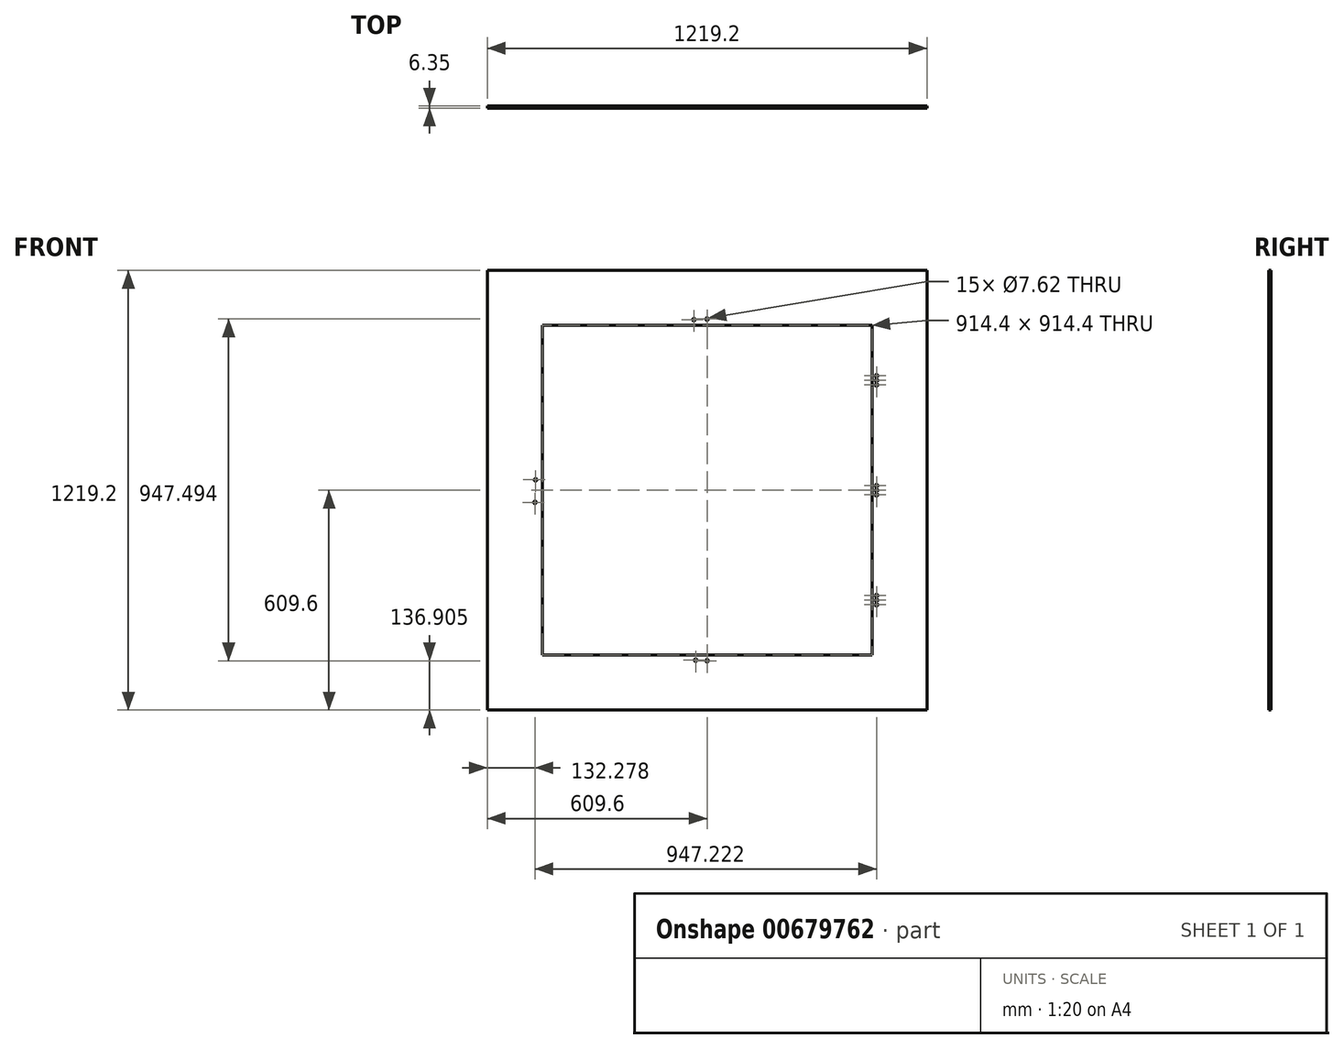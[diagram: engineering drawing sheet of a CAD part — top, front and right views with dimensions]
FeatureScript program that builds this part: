
annotation { "Feature Type Name" : "Feature", "Feature Type Description" : "" }
export const myFeature = defineFeature(function(context is Context, id is Id, definition is map)
    precondition{}
    {
        {
            var Q0;
            Q0=qCreatedBy(makeId("Front.planeOp"),FACE);
            var sketch = newSketch(context, id + "F0", { "sketchPlane" : qUnion([Q0])});
            skLineSegment(sketch, "E0.bottom", {"start": v(609.6, -609.6) * mm, "end": v(-609.6, -609.6) * mm});
            skLineSegment(sketch, "E0.top", {"start": v(609.6, 609.6) * mm, "end": v(-609.6, 609.6) * mm});
            skLineSegment(sketch, "E0.left", {"start": v(609.6, -609.6) * mm, "end": v(609.6, 609.6) * mm});
            skLineSegment(sketch, "E0.right", {"start": v(-609.6, -609.6) * mm, "end": v(-609.6, 609.6) * mm});
            skPoint(sketch, "E0.middle", {"position": v(0, 0) * mm});
            skLineSegment(sketch, "E1.bottom", {"start": v(457.2, -457.2) * mm, "end": v(-457.2, -457.2) * mm});
            skLineSegment(sketch, "E1.top", {"start": v(457.2, 457.2) * mm, "end": v(-457.2, 457.2) * mm});
            skLineSegment(sketch, "E1.left", {"start": v(457.2, -457.2) * mm, "end": v(457.2, 457.2) * mm});
            skLineSegment(sketch, "E1.right", {"start": v(-457.2, -457.2) * mm, "end": v(-457.2, 457.2) * mm});
            skLineSegment(sketch, "E2", {"start": v(469.9, 639.15) * mm, "end": v(469.9, -669.22) * mm});
            skLineSegment(sketch, "E3", {"start": v(300.82, 304.8) * mm, "end": v(457.2, 304.8) * mm});
            skLineSegment(sketch, "E4", {"start": v(303.39, 0) * mm, "end": v(457.2, 0) * mm});
            skLineSegment(sketch, "E5", {"start": v(313.4, -304.8) * mm, "end": v(457.2, -304.8) * mm});
            skPoint(sketch, "E6", {"position": v(469.9, 304.8) * mm});
            skPoint(sketch, "E7", {"position": v(469.9, 317.5) * mm});
            skPoint(sketch, "E8", {"position": v(469.9, 292.1) * mm});
            skPoint(sketch, "E9", {"position": v(469.9, 0) * mm});
            skPoint(sketch, "E10", {"position": v(469.9, 12.7) * mm});
            skPoint(sketch, "E11", {"position": v(469.9, -12.7) * mm});
            skPoint(sketch, "E12", {"position": v(469.9, -292.1) * mm});
            skPoint(sketch, "E13", {"position": v(469.9, -304.8) * mm});
            skPoint(sketch, "E14", {"position": v(469.9, -317.5) * mm});
            skLineSegment(sketch, "E15.trimOffspring", {"start": v(609.6, 304.8) * mm, "end": v(695.75, 304.8) * mm});
            skLineSegment(sketch, "E16.trimOffspring", {"start": v(609.6, 0) * mm, "end": v(667.54, 0) * mm});
            skLineSegment(sketch, "E17.trimOffspring", {"start": v(609.6, -304.8) * mm, "end": v(688.77, -304.8) * mm});
            skPoint(sketch, "E18", {"position": v(0, 474.8) * mm});
            skPoint(sketch, "E19", {"position": v(0, -472.7) * mm});
            skPoint(sketch, "E19.positionSnap0", {"position": v(0, -457.2) * mm});
            skPoint(sketch, "E20", {"position": v(-31.73, -471.09) * mm});
            skPoint(sketch, "E21", {"position": v(-477.32, -33.53) * mm});
            skPoint(sketch, "E22", {"position": v(-475.71, 29.2) * mm});
            skPoint(sketch, "E23", {"position": v(-36.55, 473.2) * mm});
            skSolve(sketch);
        }
        {
            var Q0;
            Q0 = qSketchRegion(id + "F0", true);
            extrude(context, id + "F1", {"entities" : qUnion([Q0]), "depth" : 6.35 * mm, "offsetDistance" : 30.48 * mm});
        }
        {
            var Q0;
            Q0=sQuery(id+"F0.wireOp",VERTEX,"E7");
            var Q1;
            Q1=sQuery(id+"F0.wireOp",VERTEX,"E6");
            var Q2;
            Q2=sQuery(id+"F0.wireOp",VERTEX,"E8");
            var Q3;
            Q3=sQuery(id+"F0.wireOp",VERTEX,"E10");
            var Q4;
            Q4=sQuery(id+"F0.wireOp",VERTEX,"E11");
            var Q5;
            Q5=sQuery(id+"F0.wireOp",VERTEX,"E9");
            var Q6;
            Q6=sQuery(id+"F0.wireOp",VERTEX,"E12");
            var Q7;
            Q7=sQuery(id+"F0.wireOp",VERTEX,"E13");
            var Q8;
            Q8=sQuery(id+"F0.wireOp",VERTEX,"E14");
            var Q9;
            Q9=sQuery(id+"F0.wireOp",VERTEX,"E18");
            var Q10;
            Q10=sQuery(id+"F0.wireOp",VERTEX,"E23");
            var Q11;
            Q11=sQuery(id+"F0.wireOp",VERTEX,"E22");
            var Q12;
            Q12=sQuery(id+"F0.wireOp",VERTEX,"E21");
            var Q13;
            Q13=sQuery(id+"F0.wireOp",VERTEX,"E20");
            var Q14;
            Q14=sQuery(id+"F0.wireOp",VERTEX,"E19");
            var Q15;
            Q15=makeQuery(id+"F1.opExtrude","SWEPT_BODY",BODY,{"disambiguationData":[OSD([sQuery(id+"F0.wireOp",EDGE,"E0.bottom"),sQuery(id+"F0.wireOp",EDGE,"E0.top"),sQuery(id+"F0.wireOp",EDGE,"E0.left"),sQuery(id+"F0.wireOp",EDGE,"E0.right"),sQuery(id+"F0.wireOp",EDGE,"E1.bottom"),sQuery(id+"F0.wireOp",EDGE,"E1.top"),sQuery(id+"F0.wireOp",EDGE,"E1.left"),sQuery(id+"F0.wireOp",EDGE,"E1.right")])]});
            hole(context, id + "F2", {"style" : HoleStyle.C_SINK, "endStyle" : HoleEndStyle.THROUGH, "oppositeDirection" : true, "holeDiameter" : 7.62 * mm, "cSinkDiameter" : 9.52 * mm, "cSinkAngle" : 90 * degree, "majorDiameter" : 6.35 * mm, "isTappedThrough" : true, "tappedDepth" : 12.7 * mm, "tapClearance" : 3, "locations" : qUnion([Q0, Q1, Q2, Q3, Q4, Q5, Q6, Q7, Q8, Q9, Q10, Q11, Q12, Q13, Q14]), "scope" : qUnion([Q15])});
        }
    });
